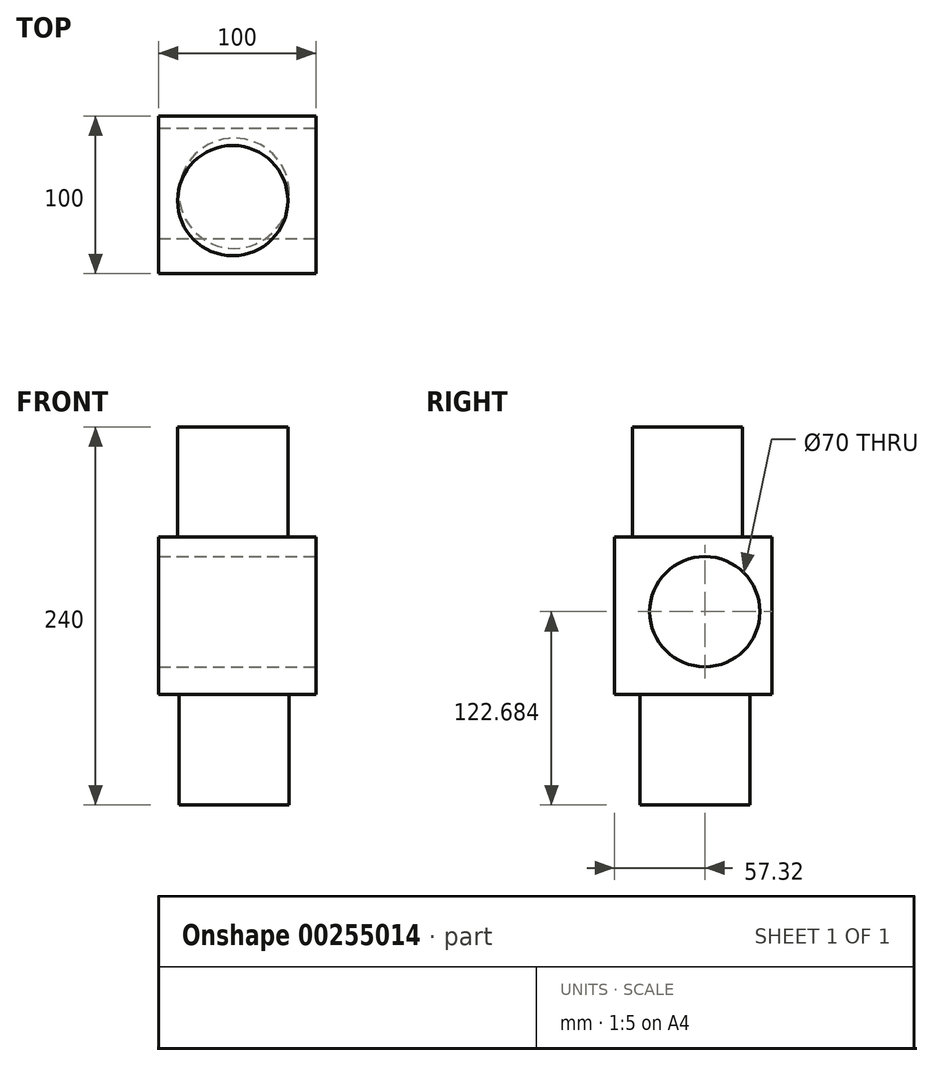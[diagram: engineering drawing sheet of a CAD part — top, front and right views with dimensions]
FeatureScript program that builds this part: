
annotation { "Feature Type Name" : "Feature", "Feature Type Description" : "" }
export const myFeature = defineFeature(function(context is Context, id is Id, definition is map)
    precondition{}
    {
        {
            var Q0;
            Q0=qCreatedBy(makeId("Front.planeOp"),FACE);
            var sketch = newSketch(context, id + "F0", { "sketchPlane" : qUnion([Q0])});
            skLineSegment(sketch, "E0.bottom", {"start": v(0, 0) * mm, "end": v(100, 0) * mm});
            skLineSegment(sketch, "E0.top", {"start": v(0, 100) * mm, "end": v(100, 100) * mm});
            skLineSegment(sketch, "E0.left", {"start": v(0, 0) * mm, "end": v(0, 100) * mm});
            skLineSegment(sketch, "E0.right", {"start": v(100, 0) * mm, "end": v(100, 100) * mm});
            skSolve(sketch);
        }
        {
            var Q0;
            Q0=makeQuery(id+"F0.imprint","IMPRINT",FACE,{"disambiguationData":[TD([[makeQuery(id+"F0.imprint","IMPRINT",EDGE,{"derivedFrom":sQuery(id+"F0.wireOp",EDGE,"E0.bottom")}),1.0]])]});
            extrude(context, id + "F1", {"entities" : qUnion([Q0]), "depth" : 100 * mm});
        }
        {
            var Q0;
            Q0=makeQuery(id+"F1.opExtrude","SWEPT_FACE",FACE,{"disambiguationData":[OSD([sQuery(id+"F0.wireOp",EDGE,"E0.bottom")])]});
            var sketch = newSketch(context, id + "F2", { "sketchPlane" : qUnion([Q0])});
            skCircle(sketch, "E1", {"center": v(48.02, 49.02) * mm, "radius": 35 * mm});
            skSolve(sketch);
        }
        {
            var Q0;
            Q0 = qSketchRegion(id + "F2", true);
            extrude(context, id + "F3", {"entities" : qUnion([Q0]), "operationType" : NewBodyOperationType.ADD, "depth" : 70 * mm});
        }
        {
            var Q0;
            Q0=makeQuery(id+"F1.opExtrude","SWEPT_FACE",FACE,{"disambiguationData":[OSD([sQuery(id+"F0.wireOp",EDGE,"E0.top")])]});
            var sketch = newSketch(context, id + "F4", { "sketchPlane" : qUnion([Q0])});
            skCircle(sketch, "E2", {"center": v(47.1, -53.72) * mm, "radius": 35 * mm});
            skSolve(sketch);
        }
        {
            var Q0;
            Q0 = qSketchRegion(id + "F4", true);
            extrude(context, id + "F5", {"entities" : qUnion([Q0]), "operationType" : NewBodyOperationType.ADD, "depth" : 70 * mm});
        }
        {
            var Q0;
            Q0=makeQuery(id+"F1.opExtrude","SWEPT_FACE",FACE,{"disambiguationData":[OSD([sQuery(id+"F0.wireOp",EDGE,"E0.right")])]});
            var sketch = newSketch(context, id + "F6", { "sketchPlane" : qUnion([Q0])});
            skCircle(sketch, "E3", {"center": v(-42.68, 52.68) * mm, "radius": 35 * mm});
            skSolve(sketch);
        }
        {
            var Q0;
            Q0=sQuery(id+"F6.wireOp",VERTEX,"E3.center");
            var Q1;
            Q1=makeQuery(id+"F1.opExtrude","SWEPT_BODY",BODY,{"disambiguationData":[OSD([sQuery(id+"F0.wireOp",EDGE,"E0.bottom"),sQuery(id+"F0.wireOp",EDGE,"E0.top"),sQuery(id+"F0.wireOp",EDGE,"E0.left"),sQuery(id+"F0.wireOp",EDGE,"E0.right")])]});
            hole(context, id + "F7", {"style" : HoleStyle.SIMPLE, "endStyle" : HoleEndStyle.THROUGH, "holeDiameter" : 70 * mm, "tappedDepth" : 12 * mm, "tapClearance" : 3, "locations" : qUnion([Q0]), "scope" : qUnion([Q1])});
        }
    });
